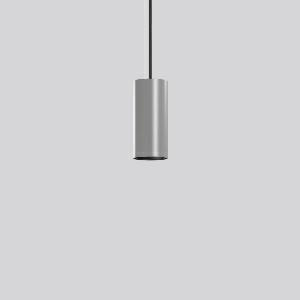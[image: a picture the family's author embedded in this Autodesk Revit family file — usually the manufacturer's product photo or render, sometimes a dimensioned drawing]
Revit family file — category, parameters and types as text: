
# Revit family: deecos_p_mini_911522_004_2_df79
name_source: partatom
category: Lighting Fixtures
units: mm (PartAtom-declared; Revit-internal decimal feet)

## family parameters
Cut with Voids When Loaded = No
Host = Face
Light Source = No
Part Type = Normal
Room Calculation Point = No
Round Connector Dimension = Use Diameter
Shared = No

## types (1)
- DEECOS P mini (1 x LED Modul 927, 3300 lm, 2700)
    Apparent Load = 29 VA
    Approval mark = CE
    CIE Flux Codes = 99 100 100 100 100
    Color Rendering = 92
    Color Temperature = 2700
    Default Elevation = 1800 mm
    Description = Series: DEECOS P mini
Cylindrical pendant luminaire. Housing: die-cast aluminium, powder-coated. Canopy made of powder-coated sheet steel with magnetic attachment. Optical assembly with reflector made of MIRO-Silver with 98% total light reflection for outstanding efficiency - can be changed without tools. Best colour rendering index Ra>90. Transparent pendant cable 5 m, can be shortened, with integrated steel cable. High quality converter without flickering and stroboscopic effect. The following accessories can be mounted without use of tools: interchangeable lenses, honeycomb louvre, clear and frosted diffusers, white interchangeable plastic ring. Decorative recessed suspension set available as accessory.Suitable for accessory Deecos P Tube cylinder extensions 0.5 m, 0.75 m or 1 m. 
Colour: silver
Diameter: 87 mm
Height: 195 mm
Suspension length: 5000 mm
Lamp: LED
Socket: without socket
Colour temperature: 2700K
Colour rendering index (CRI): 92
System power: 29 W
Rated luminous flux: 3300 lm
Luminous efficiency: 114 lm/W
Control gear: Regulated power supply
Protection class: I
Type of protection: IP 20
    Height = 195 mm
    Lamp = 1 x LED Modul 927
    Lamp Light Flux = 3300 lm
    Lamp count = 1
    Length = 87 mm
    Lifetime = 50000 h
    Luminous efficacy = 114 lm/W
    Manufacturer = RZB
    ModVariant = No
    Model = 911522.004.2
    Mounting Place = Ceiling
    Mounting Type = Pendant
    Number of Poles = 1
    OnlyDefault = Yes
    Power Factor = 1
    Product Name = DEECOS P mini
    Product group = Pendant luminaires
    ProductGroupID = 902
    Protection Class = Protection class I
    Protection Degree = IP 20
    RLX_Detail_Level = 1
    RLX_Emergency_Light_Flux = 0 lm
    RLX_Emergency_Type = 0
    RLX_Emergency_Type_DB = No
    RlxData = <blob elided: 55497 chars, md5=126aa511>
    Socket = socket
    Standby Power = 0 W
    System Light Flux = 3300 lm
    System Power = 29 W
    Type Comments = Product without accessories
    Type Image = 911476.004.jpg
    URL = http://relux.com
    VarID = ---
    Voltage = 230 V
    Voltage Range = 220-240 V
    Weight = 0.00 kg
    Width = 0 mm  [stored 0 ft]

note: [stored X ft] marks values corroborated as IEEE doubles in the binary element streams (Revit-internal decimal feet)

## geometry (parser evidence)
native form markers: Blend x4, Sweep x12
no freeform markers — native parametric forms only
